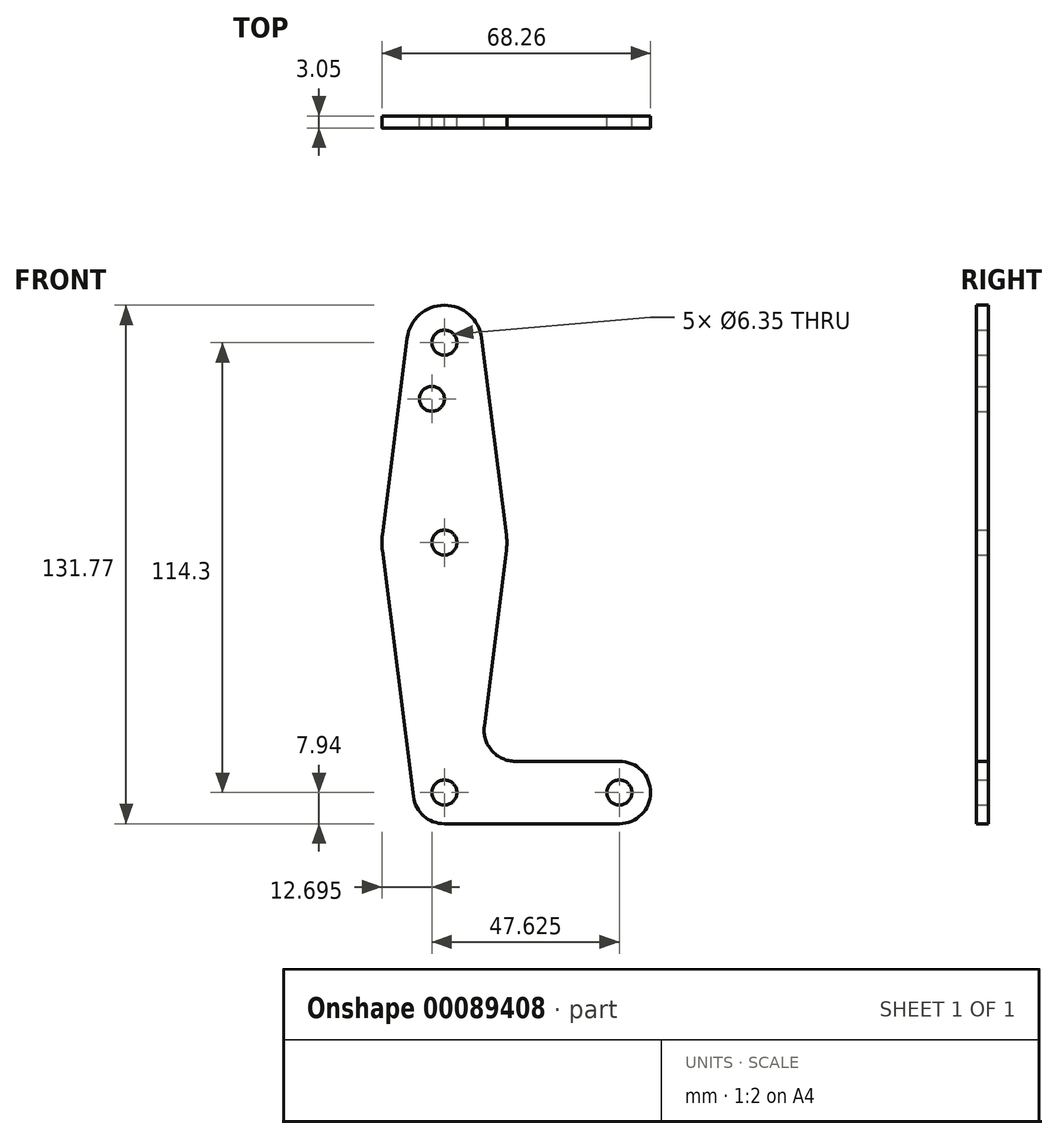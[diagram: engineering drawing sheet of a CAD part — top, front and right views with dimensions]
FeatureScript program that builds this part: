
annotation { "Feature Type Name" : "Feature", "Feature Type Description" : "" }
export const myFeature = defineFeature(function(context is Context, id is Id, definition is map)
    precondition{}
    {
        {
            var Q0;
            Q0=qCreatedBy(makeId("Front.planeOp"),FACE);
            var sketch = newSketch(context, id + "F0", { "sketchPlane" : qUnion([Q0])});
            skLineSegment(sketch, "E0", {"start": v(0, 114.3) * mm, "end": v(0, 0) * mm, "construction": true});
            skLineSegment(sketch, "E1", {"start": v(0, 0) * mm, "end": v(44.45, 0) * mm});
            skCircle(sketch, "E2", {"center": v(0, 114.3) * mm, "radius": 9.53 * mm});
            skCircle(sketch, "E3", {"center": v(0, 63.5) * mm, "radius": 15.88 * mm});
            skCircle(sketch, "E4", {"center": v(0, 0) * mm, "radius": 7.94 * mm});
            skCircle(sketch, "E5", {"center": v(44.45, 0) * mm, "radius": 7.94 * mm});
            skLineSegment(sketch, "E6", {"start": v(0, -7.94) * mm, "end": v(44.45, -7.94) * mm});
            skLineSegment(sketch, "E7", {"start": v(18.01, 7.94) * mm, "end": v(44.45, 7.94) * mm});
            skLineSegment(sketch, "E8", {"start": v(-9.45, 115.5) * mm, "end": v(-15.75, 65.48) * mm});
            skLineSegment(sketch, "E9", {"start": v(9.45, 115.5) * mm, "end": v(15.75, 65.48) * mm});
            skLineSegment(sketch, "E10", {"start": v(15.75, 61.52) * mm, "end": v(10.13, 16.88) * mm});
            skCircle(sketch, "E11", {"center": v(0, 114.3) * mm, "radius": 3.18 * mm});
            skCircle(sketch, "E12", {"center": v(0, 63.5) * mm, "radius": 3.18 * mm});
            skCircle(sketch, "E13", {"center": v(0, 0) * mm, "radius": 3.18 * mm});
            skCircle(sketch, "E14", {"center": v(44.45, 0) * mm, "radius": 3.18 * mm});
            skCircle(sketch, "E15", {"center": v(-3.18, 100.03) * mm, "radius": 3.18 * mm});
            skPoint(sketch, "E16.newPointB", {"position": v(0, 7.94) * mm});
            skArc(sketch, "E16.filletArc", {"start": v(10.13, 16.88) * mm, "mid": v(12.05, 10.63) * mm, "end": v(18.01, 7.94) * mm});
            skLineSegment(sketch, "E17", {"start": v(-15.75, 61.52) * mm, "end": v(-7.88, -1) * mm});
            skLineSegment(sketch, "E18", {"start": v(-3.18, 100.03) * mm, "end": v(-3.18, 63.66) * mm});
            skLineSegment(sketch, "E19", {"start": v(-3.18, 100.03) * mm, "end": v(0, 100.03) * mm});
            skSolve(sketch);
        }
        {
            var Q0;
            Q0 = qSketchRegion(id + "F0", true);
            extrude(context, id + "F1", {"entities" : qUnion([Q0]), "depth" : 3.05 * mm});
        }
    });
